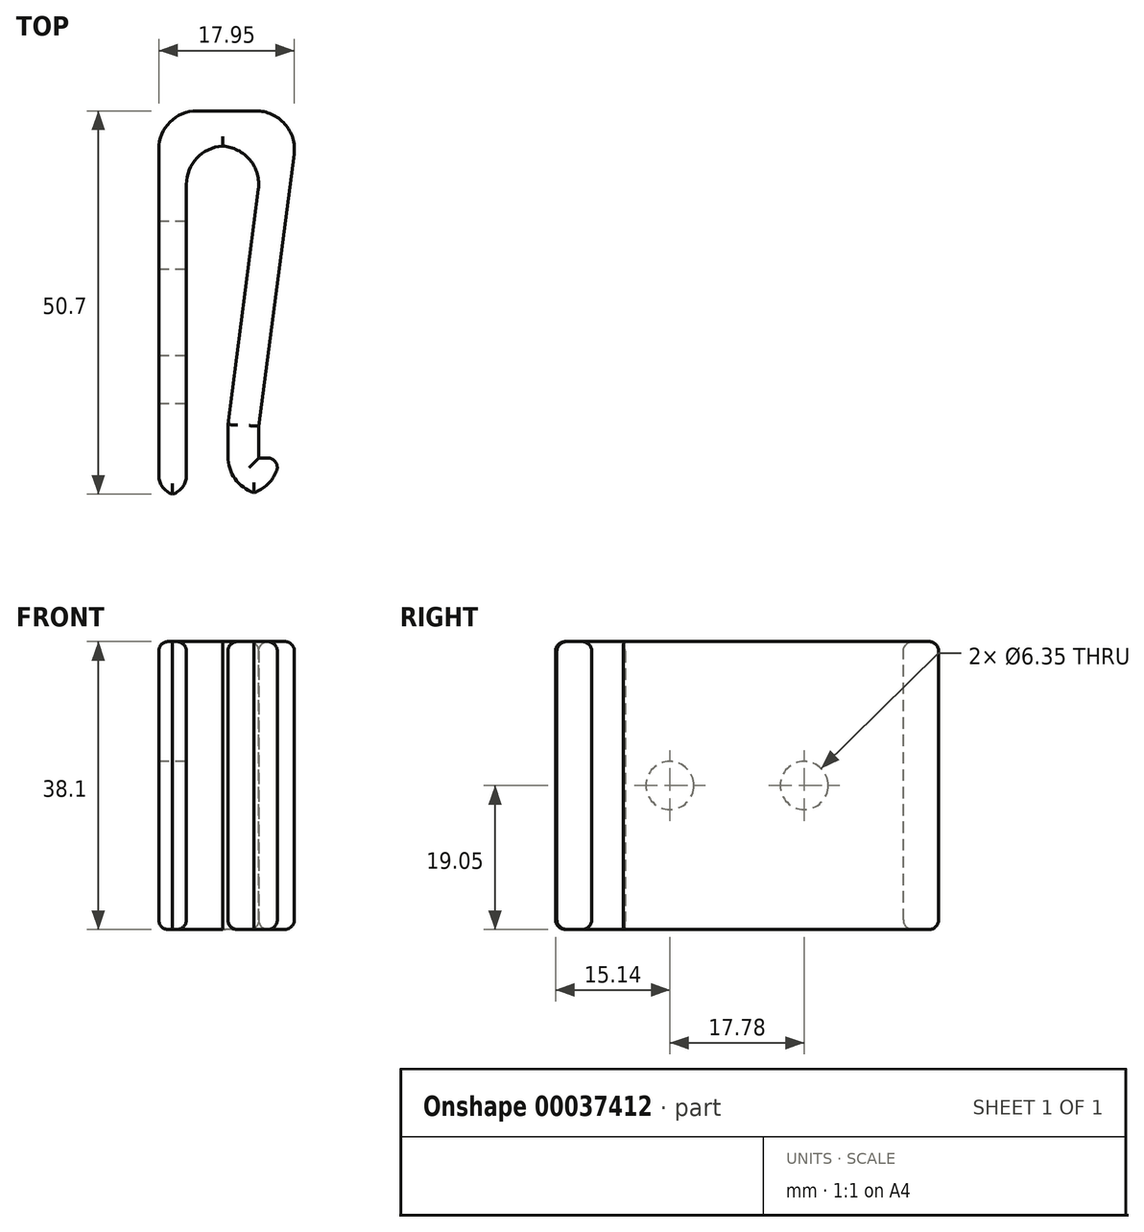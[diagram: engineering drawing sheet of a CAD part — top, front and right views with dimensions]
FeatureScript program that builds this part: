
annotation { "Feature Type Name" : "Feature", "Feature Type Description" : "" }
export const myFeature = defineFeature(function(context is Context, id is Id, definition is map)
    precondition{}
    {
        {
            var Q0;
            Q0=qCreatedBy(makeId("Top.planeOp"),FACE);
            var sketch = newSketch(context, id + "F0", { "sketchPlane" : qUnion([Q0])});
            skLineSegment(sketch, "E0", {"start": v(0, 0) * mm, "end": v(0, 50.8) * mm});
            skLineSegment(sketch, "E1", {"start": v(0, 50.8) * mm, "end": v(18.65, 50.8) * mm});
            skLineSegment(sketch, "E2", {"start": v(18.65, 50.8) * mm, "end": v(13.25, 9.08) * mm});
            skLineSegment(sketch, "E3", {"start": v(0, 0) * mm, "end": v(3.66, 0) * mm});
            skLineSegment(sketch, "E4", {"start": v(3.66, 0) * mm, "end": v(3.66, 46.15) * mm});
            skLineSegment(sketch, "E5", {"start": v(3.66, 46.15) * mm, "end": v(13.93, 46.15) * mm});
            skLineSegment(sketch, "E6", {"start": v(13.93, 46.15) * mm, "end": v(9.16, 9.3) * mm});
            skLineSegment(sketch, "E7", {"start": v(9.16, 9.3) * mm, "end": v(9.16, 0) * mm});
            skLineSegment(sketch, "E8", {"start": v(9.16, 0) * mm, "end": v(15.98, 0) * mm});
            skLineSegment(sketch, "E9", {"start": v(15.98, 0) * mm, "end": v(15.98, 4.89) * mm});
            skLineSegment(sketch, "E10", {"start": v(15.98, 4.89) * mm, "end": v(13.25, 4.89) * mm});
            skLineSegment(sketch, "E11", {"start": v(13.25, 4.89) * mm, "end": v(13.25, 9.08) * mm});
            skSolve(sketch);
        }
        {
            var Q0;
            Q0 = qSketchRegion(id + "F0", true);
            extrude(context, id + "F1", {"entities" : qUnion([Q0]), "depth" : 38.1 * mm});
        }
        {
            var Q0;
            Q0=makeQuery(id+"F1.opExtrude","SWEPT_FACE",FACE,{"disambiguationData":[OSD([sQuery(id+"F0.wireOp",EDGE,"E0")])]});
            var sketch = newSketch(context, id + "F2", { "sketchPlane" : qUnion([Q0])});
            skLineSegment(sketch, "E12", {"start": v(-50.8, 19.05) * mm, "end": v(-33.02, 19.05) * mm});
            skLineSegment(sketch, "E13", {"start": v(-33.02, 19.05) * mm, "end": v(-15.24, 19.05) * mm});
            skCircle(sketch, "E14", {"center": v(-33.02, 19.05) * mm, "radius": 3.18 * mm});
            skCircle(sketch, "E15", {"center": v(-15.24, 19.05) * mm, "radius": 3.18 * mm});
            skSolve(sketch);
        }
        {
            var Q0;
            Q0 = qSketchRegion(id + "F2", true);
            extrude(context, id + "F3", {"entities" : qUnion([Q0]), "operationType" : NewBodyOperationType.REMOVE, "oppositeDirection" : true, "depth" : 5.08 * mm});
        }
        {
            var Q0;
            Q0=makeQuery(id+"F1.opExtrude","SWEPT_EDGE",EDGE,{"disambiguationData":[OSD([sQuery(id+"F0.wireOp",EDGE,"E0"),sQuery(id+"F0.wireOp",EDGE,"E1")])]});
            var Q1;
            Q1=makeQuery(id+"F1.opExtrude","SWEPT_EDGE",EDGE,{"disambiguationData":[OSD([sQuery(id+"F0.wireOp",EDGE,"E1"),sQuery(id+"F0.wireOp",EDGE,"E2")])]});
            var Q2;
            Q2=makeQuery(id+"F1.opExtrude","SWEPT_EDGE",EDGE,{"disambiguationData":[OSD([sQuery(id+"F0.wireOp",EDGE,"E5"),sQuery(id+"F0.wireOp",EDGE,"E6")])]});
            var Q3;
            Q3=makeQuery(id+"F1.opExtrude","SWEPT_EDGE",EDGE,{"disambiguationData":[OSD([sQuery(id+"F0.wireOp",EDGE,"E4"),sQuery(id+"F0.wireOp",EDGE,"E5")])]});
            var Q4;
            Q4=makeQuery(id+"F1.opExtrude","SWEPT_EDGE",EDGE,{"disambiguationData":[OSD([sQuery(id+"F0.wireOp",EDGE,"E7"),sQuery(id+"F0.wireOp",EDGE,"E8")])]});
            var Q5;
            Q5=makeQuery(id+"F1.opExtrude","SWEPT_EDGE",EDGE,{"disambiguationData":[OSD([sQuery(id+"F0.wireOp",EDGE,"E8"),sQuery(id+"F0.wireOp",EDGE,"E9")])]});
            fillet(context, id + "F4", {"entities" : qUnion([Q0, Q1, Q2, Q3, Q4, Q5]), "radius" : 5.08 * mm, "tangentPropagation" : true, "allowEdgeOverflow" : false});
        }
        {
            var Q0;
            Q0=makeQuery(id+"F1.opExtrude","SWEPT_EDGE",EDGE,{"disambiguationData":[OSD([sQuery(id+"F0.wireOp",EDGE,"E3"),sQuery(id+"F0.wireOp",EDGE,"E4")])]});
            var Q1;
            Q1=makeQuery(id+"F1.opExtrude","SWEPT_EDGE",EDGE,{"disambiguationData":[OSD([sQuery(id+"F0.wireOp",EDGE,"E0"),sQuery(id+"F0.wireOp",EDGE,"E3")])]});
            fillet(context, id + "F5", {"entities" : qUnion([Q0, Q1]), "radius" : 2.54 * mm, "tangentPropagation" : true, "allowEdgeOverflow" : false});
        }
        {
            var Q0;
            Q0=makeQuery(id+"F1.opExtrude","CAP_FACE",FACE,{"disambiguationData":[OSD([sQuery(id+"F0.wireOp",EDGE,"E0"),sQuery(id+"F0.wireOp",EDGE,"E1"),sQuery(id+"F0.wireOp",EDGE,"E2"),sQuery(id+"F0.wireOp",EDGE,"E3"),sQuery(id+"F0.wireOp",EDGE,"E4"),sQuery(id+"F0.wireOp",EDGE,"E5"),sQuery(id+"F0.wireOp",EDGE,"E6"),sQuery(id+"F0.wireOp",EDGE,"E7"),sQuery(id+"F0.wireOp",EDGE,"E8"),sQuery(id+"F0.wireOp",EDGE,"E9"),sQuery(id+"F0.wireOp",EDGE,"E10"),sQuery(id+"F0.wireOp",EDGE,"E11")])],"isStart":true});
            var Q1;
            Q1=makeQuery(id+"F1.opExtrude","CAP_FACE",FACE,{"disambiguationData":[OSD([sQuery(id+"F0.wireOp",EDGE,"E0"),sQuery(id+"F0.wireOp",EDGE,"E1"),sQuery(id+"F0.wireOp",EDGE,"E2"),sQuery(id+"F0.wireOp",EDGE,"E3"),sQuery(id+"F0.wireOp",EDGE,"E4"),sQuery(id+"F0.wireOp",EDGE,"E5"),sQuery(id+"F0.wireOp",EDGE,"E6"),sQuery(id+"F0.wireOp",EDGE,"E7"),sQuery(id+"F0.wireOp",EDGE,"E8"),sQuery(id+"F0.wireOp",EDGE,"E9"),sQuery(id+"F0.wireOp",EDGE,"E10"),sQuery(id+"F0.wireOp",EDGE,"E11")])],"isStart":false});
            fillet(context, id + "F6", {"entities" : qUnion([Q0, Q1]), "radius" : 1.27 * mm, "tangentPropagation" : true, "allowEdgeOverflow" : false});
        }
        {
            var Q0;
            Q0=makeQuery(id+"F4.opFillet","BLEND_EDGE",EDGE,{"blendedFrom":[makeQuery(id+"F1.opExtrude","SWEPT_EDGE",EDGE,{"disambiguationData":[OSD([sQuery(id+"F0.wireOp",EDGE,"E8"),sQuery(id+"F0.wireOp",EDGE,"E9")])]}),makeQuery(id+"F1.opExtrude","SWEPT_FACE",FACE,{"disambiguationData":[OSD([sQuery(id+"F0.wireOp",EDGE,"E10")])]})],"blendedInto":[makeQuery(id+"F1.opExtrude","SWEPT_FACE",FACE,{"disambiguationData":[OSD([sQuery(id+"F0.wireOp",EDGE,"E10")])]})]});
            fillet(context, id + "F7", {"entities" : qUnion([Q0]), "radius" : 1.27 * mm, "tangentPropagation" : true, "allowEdgeOverflow" : false});
        }
    });
